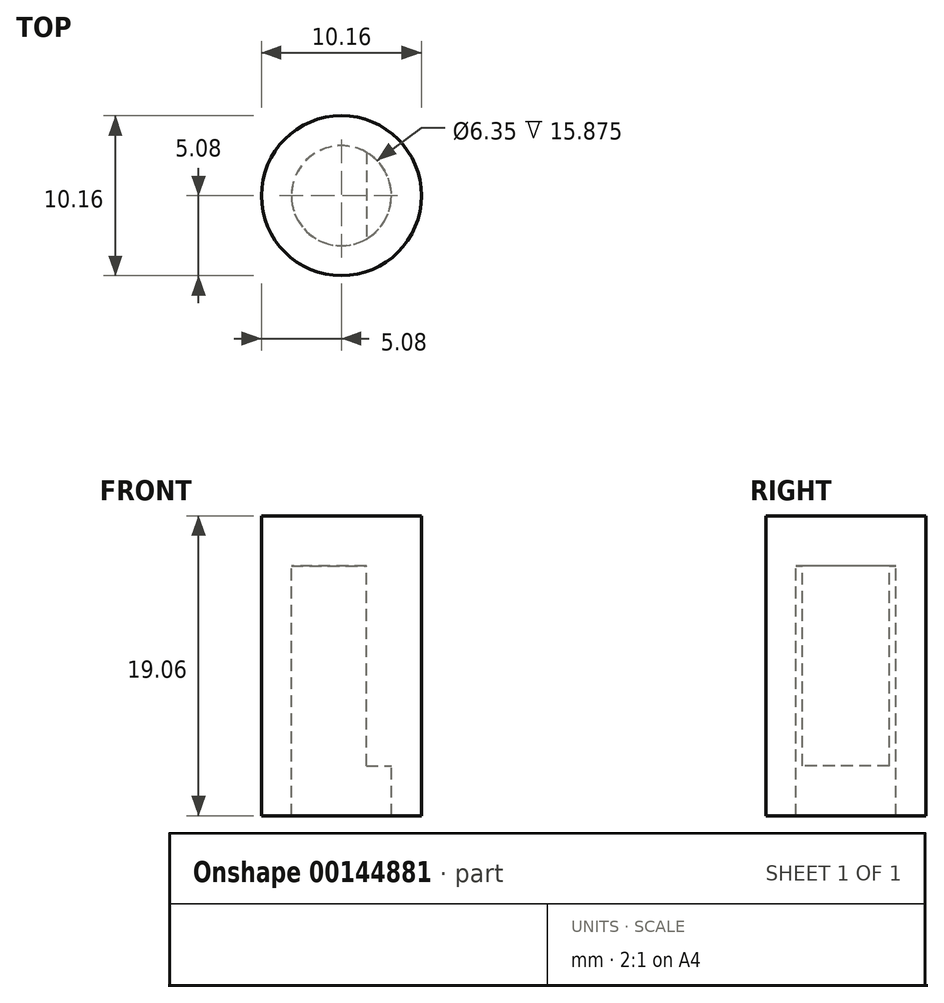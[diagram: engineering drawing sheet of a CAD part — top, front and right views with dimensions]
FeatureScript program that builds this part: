
annotation { "Feature Type Name" : "Feature", "Feature Type Description" : "" }
export const myFeature = defineFeature(function(context is Context, id is Id, definition is map)
    precondition{}
    {
        {
            var Q0;
            Q0=qCreatedBy(makeId("Top.planeOp"),FACE);
            var sketch = newSketch(context, id + "F0", { "sketchPlane" : qUnion([Q0])});
            skCircle(sketch, "E0", {"center": v(0, 0) * mm, "radius": 5.08 * mm});
            skSolve(sketch);
        }
        {
            var Q0;
            Q0=makeQuery(id+"F0.imprint","IMPRINT",FACE,{"disambiguationData":[TD([[makeQuery(id+"F0.imprint","IMPRINT",EDGE,{"derivedFrom":sQuery(id+"F0.wireOp",EDGE,"E0")}),1.0]])]});
            extrude(context, id + "F1", {"entities" : qUnion([Q0]), "depth" : 12.7 * mm});
        }
        {
            var Q0;
            Q0=makeQuery(id+"F1.opExtrude","CAP_FACE",FACE,{"disambiguationData":[OSD([sQuery(id+"F0.wireOp",EDGE,"E0")])],"isStart":false});
            var sketch = newSketch(context, id + "F2", { "sketchPlane" : qUnion([Q0])});
            skCircle(sketch, "E1", {"center": v(0, 0) * mm, "radius": 3.18 * mm});
            skPoint(sketch, "E2", {"position": v(1.59, 0) * mm});
            skLineSegment(sketch, "E3", {"start": v(1.59, 2.75) * mm, "end": v(1.59, -2.75) * mm});
            skSolve(sketch);
        }
        {
            var Q0;
            {var subQ0=sQuery(id+"F2.wireOp",EDGE,"E3");Q0=makeQuery(id+"F2.imprint","IMPRINT",FACE,{"disambiguationData":[TD([[makeQuery(id+"F2.imprint","IMPRINT",EDGE,{"derivedFrom":subQ0}),-1.0]])]});}
            extrude(context, id + "F3", {"entities" : qUnion([Q0]), "operationType" : NewBodyOperationType.REMOVE, "oppositeDirection" : true, "depth" : 25.4 * mm});
        }
        {
            var Q0;
            Q0=makeQuery(id+"F1.opExtrude","CAP_FACE",FACE,{"disambiguationData":[OSD([sQuery(id+"F0.wireOp",EDGE,"E0")])],"isStart":false});
            var sketch = newSketch(context, id + "F4", { "sketchPlane" : qUnion([Q0])});
            skCircle(sketch, "E4", {"center": v(0, 0) * mm, "radius": 5.08 * mm});
            skSolve(sketch);
        }
        {
            var Q0;
            Q0 = qSketchRegion(id + "F4", true);
            extrude(context, id + "F5", {"entities" : qUnion([Q0]), "operationType" : NewBodyOperationType.ADD, "depth" : 3.17 * mm});
        }
        {
            var Q0;
            Q0=makeQuery(id+"F1.opExtrude","CAP_FACE",FACE,{"disambiguationData":[OSD([sQuery(id+"F0.wireOp",EDGE,"E0")])],"isStart":true});
            var sketch = newSketch(context, id + "F6", { "sketchPlane" : qUnion([Q0])});
            skCircle(sketch, "E5", {"center": v(0, 0) * mm, "radius": 5.08 * mm});
            skSolve(sketch);
        }
        {
            var Q0;
            Q0 = qSketchRegion(id + "F6", true);
            extrude(context, id + "F7", {"entities" : qUnion([Q0]), "operationType" : NewBodyOperationType.ADD, "depth" : 3.17 * mm});
        }
        {
            var Q0;
            Q0=makeQuery(id+"F7.opExtrude","CAP_FACE",FACE,{"disambiguationData":[OSD([sQuery(id+"F6.wireOp",EDGE,"E5")])],"isStart":false});
            var sketch = newSketch(context, id + "F8", { "sketchPlane" : qUnion([Q0])});
            skCircle(sketch, "E6", {"center": v(0, 0) * mm, "radius": 3.17 * mm});
            skSolve(sketch);
        }
        {
            var Q0;
            Q0=makeQuery(id+"F8.imprint","IMPRINT",FACE,{"disambiguationData":[TD([[makeQuery(id+"F8.imprint","IMPRINT",EDGE,{"derivedFrom":sQuery(id+"F8.wireOp",EDGE,"E6")}),1.0]])]});
            extrude(context, id + "F9", {"entities" : qUnion([Q0]), "operationType" : NewBodyOperationType.REMOVE, "oppositeDirection" : true, "depth" : 3.17 * mm});
        }
    });
